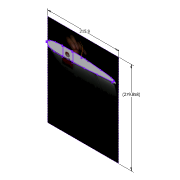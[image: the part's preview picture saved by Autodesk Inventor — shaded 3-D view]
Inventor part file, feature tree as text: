
AUTODESK INVENTOR PART (.ipt)
format: ipt  version: 2022 (Build 260153000, 153)  size: 3,058,688 bytes
history: native  units: mm
features: sketch x1, other x1
ambient origin geometry x8: Origin, YZ Plane, XZ Plane, XY Plane, X Axis, Y Axis, Z Axis, Center Point
feature tree (2):
  sketch  "Sketch1"  dims[d4=215.9mm d5=279.858004mm d8=30.0mm]
  other  "Image1"
